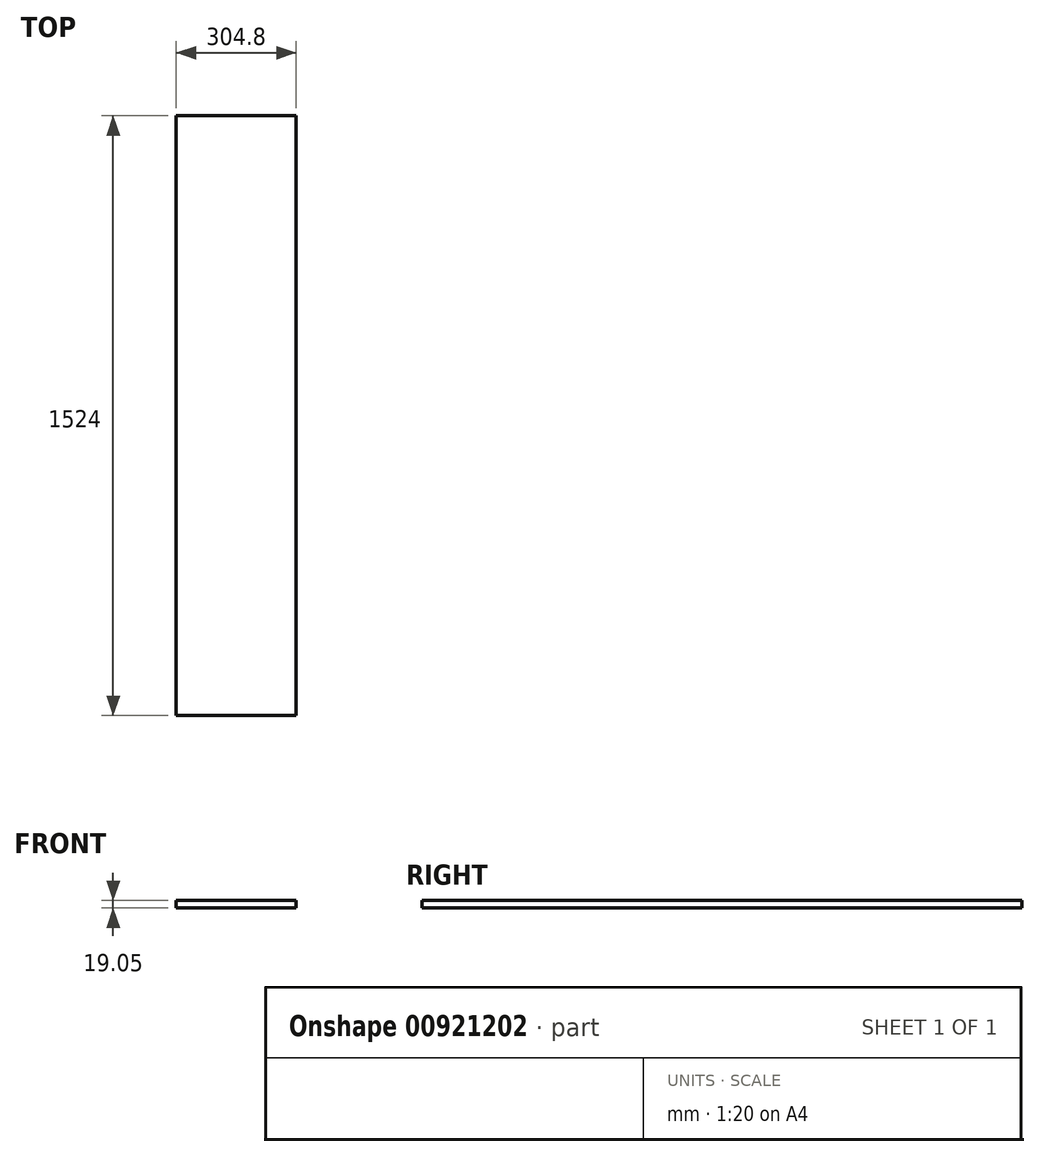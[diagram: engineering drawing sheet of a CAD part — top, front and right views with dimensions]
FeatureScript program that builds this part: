
annotation { "Feature Type Name" : "Feature", "Feature Type Description" : "" }
export const myFeature = defineFeature(function(context is Context, id is Id, definition is map)
    precondition{}
    {
        {
            var Q0;
            Q0=qCreatedBy(makeId("Front.planeOp"),FACE);
            var sketch = newSketch(context, id + "F0", { "sketchPlane" : qUnion([Q0])});
            skLineSegment(sketch, "E0.bottom", {"start": v(0, 0) * mm, "end": v(304.8, 0) * mm});
            skLineSegment(sketch, "E0.top", {"start": v(0, 19.05) * mm, "end": v(304.8, 19.05) * mm});
            skLineSegment(sketch, "E0.left", {"start": v(0, 0) * mm, "end": v(0, 19.05) * mm});
            skLineSegment(sketch, "E0.right", {"start": v(304.8, 0) * mm, "end": v(304.8, 19.05) * mm});
            skSolve(sketch);
        }
        {
            var Q0;
            Q0 = qSketchRegion(id + "F0", true);
            extrude(context, id + "F1", {"entities" : qUnion([Q0]), "depth" : 1524 * mm, "offsetDistance" : 25.4 * mm});
        }
    });
